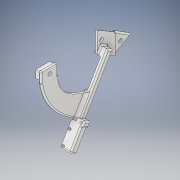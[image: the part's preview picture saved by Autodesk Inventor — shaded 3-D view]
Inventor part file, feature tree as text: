
AUTODESK INVENTOR PART (.ipt)
format: ipt  version: 2019 (Build 230136000, 136)  size: 952,832 bytes
history: native  units: mm
features: fillet x24, sketch x15, extrude x14, pattern_circular x3
ambient origin geometry x8: Origin, YZ Plane, XZ Plane, XY Plane, X Axis, Y Axis, Z Axis, Center Point
bodies: Body1 (feature_tree)
feature tree (56):
  extrude  "Extrusion5"  TaperAngle=120.0deg  [1 undecoded]
  extrude  "Extrusion6"  Depth=5.0mm TaperAngle=0.0deg
  extrude  "Extrusion7"  TaperAngle=60.0deg  [1 undecoded]
  sketch  "Sketch8"  dims[d31=20.0mm d32=60.0deg]
  extrude  "Extrusion10"  TaperAngle=60.0deg  [1 undecoded]
  extrude  "Extrusion11"  Depth=5.5mm
  extrude  "Extrusion12"  Depth=5.5mm
  sketch  "Sketch14"  dims[d40=5.0mm d41=0.0mm d42=95.981mm]
  extrude  "Extrusion13"  Depth=3.0mm
  extrude  "Extrusion14"  Depth=95.981mm
  pattern_circular  "Circular Pattern3"  Count=9  [1 undecoded]
  fillet  "Fillet2"  Radius=15.0mm
  fillet  "Fillet3"  Radius=30.0mm
  fillet  "Fillet4"  Radius=10.0mm
  fillet  "Fillet5"  Radius=2.5mm
  fillet  "Fillet6"  Radius=3.0mm
  fillet  "Fillet7"  Radius=3.5mm
  fillet  "Fillet8"  Radius=19.175mm
  fillet  "Fillet9"  Radius=2.5mm
  fillet  "Fillet10"  Radius=33.679mm
  fillet  "Fillet11"  Radius=10.775mm
  extrude  "Extrusion16"  TaperAngle=180.0deg  [1 undecoded]
  fillet  "Fillet17"  Radius=7.0mm
  fillet  "Fillet18"  Radius=3.5mm
  fillet  "Fillet19"  Radius=10.0mm
  fillet  "Fillet20"  Radius=3.5mm
  fillet  "Fillet21"  Radius=10.0mm
  pattern_circular  "Circular Pattern4"  Count=3 Angle=360.0deg
  fillet  "Fillet22"  Radius=2.0mm
  fillet  "Fillet23"  Radius=2.0mm
  fillet  "Fillet24"  Radius=2.0mm
  fillet  "Fillet25"  Radius=2.0mm
  fillet  "Fillet26"  Radius=2.0mm
  fillet  "Fillet27"  Radius=2.0mm
  extrude  "Extrusion17"  Depth=2.0mm
  pattern_circular  "Circular Pattern5"  [2 undecoded]
  extrude  "Extrusion18"  Depth=2.0mm
  extrude  "Extrusion19"  Depth=2.0mm
  extrude  "Extrusion20"  Depth=100.0mm
  extrude  "Extrusion21"  TaperAngle=180.0deg  [1 undecoded]
  fillet  "Fillet28"  Radius=5.0mm
  fillet  "Fillet29"  Radius=10.0mm
  fillet  "Fillet30"  Radius=15.0mm
  sketch  "Sketch5"  dims[d24=60.0mm d25=120.0deg]
  sketch  "Sketch6"  dims[d26=120.0deg d27=5.0mm d28=0.0mm]
  sketch  "Sketch7"  dims[d29=20.0mm d30=60.0deg]
  sketch  "Sketch11"  dims[d33=20.0mm d34=5.5mm]
  sketch  "Sketch12"  dims[d35=5.5mm d36=5.5mm]
  sketch  "Sketch13"  dims[d37=5.0mm d38=0.0mm d39=3.0mm]
  sketch  "Sketch15"  dims[d43=120.0deg]
  sketch  "Sketch16"  dims[d54=6.0mm]
  sketch  "Sketch17"  dims[d55=10.0mm]
  sketch  "Sketch18"  dims[d56=5.0mm]
  sketch  "Sketch19"  dims[d57=45.0deg]
  sketch  "Sketch20"  dims[d58=10.0mm d59=0.0mm]
  sketch  "Sketch21"  dims[d60=5.0mm d61=90.0mm d62=0.0mm d63=15.0mm d64=30.0mm d65=10.0mm d66=0.0mm d67=2.5mm d68=3.0mm d69=3.5mm d70=19.175mm d71=2.5mm d72=33.679mm d73=10.775mm d74=180.0deg d75=7.0mm d76=3.5mm d77=10.0mm d78=0.0mm d79=3.5mm d80=10.0mm d81=0.0mm d82=30.0mm d83=360.0deg d85=2.0mm d86=2.0mm d87=2.0mm d88=2.0mm d89=2.0mm d90=2.0mm d91=2.0mm d92=2.0mm d93=2.0mm d94=2.0mm d95=100.0mm d96=180.0deg d97=5.0mm d98=10.0mm d99=15.0mm d107=80.0mm d108=120.0deg d109=5.0mm d110=0.0mm d111=5.0mm d112=2.0mm d113=2.0mm d114=2.0mm d115=2.0mm d116=30.0mm d117=360.0deg d119=5.0mm d120=5.0mm d121=5.0mm d122=2.0mm d123=2.0mm d124=2.0mm d125=20.0mm d126=60.0deg d127=5.0mm d128=0.0mm d129=30.0mm d130=360.0deg d132=200.0mm d133=200.0mm d134=6.457718mm d135=24.43461mm d136=50.0mm d137=0.0mm d138=2.6mm d139=0.0mm d140=28.509mm d141=150.0deg d142=20.0mm d143=120.0deg d144=5.5mm d145=2.5mm d146=0.0mm d147=3.0mm d148=20.0mm d149=0.0mm d150=2.0mm d151=2.0mm d152=2.0mm]
note: 8 required parameter values undecoded (feature->parameter linkage not recoverable at this tier; creation-order binding heuristic only, values carry confidence <= 0.55)
